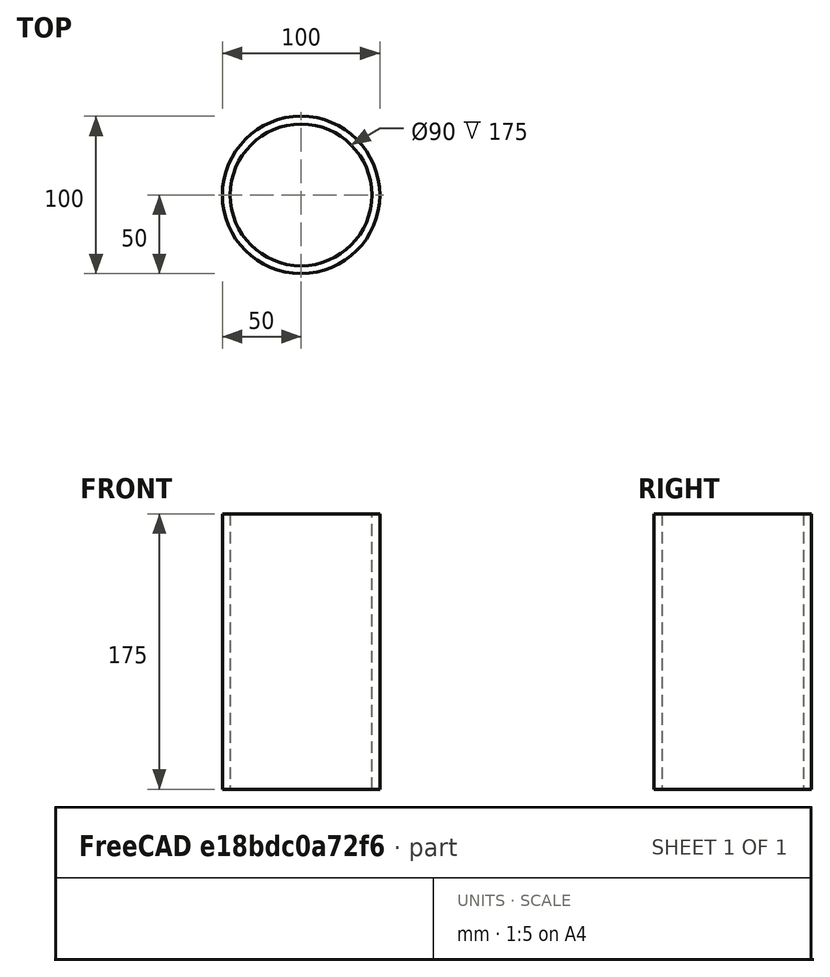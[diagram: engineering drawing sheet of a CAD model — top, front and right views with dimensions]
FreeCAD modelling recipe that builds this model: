
FCSTD DOCUMENT  (FreeCAD 0.18R16268 (Git))
Label: Cylindre
License: All rights reserved
LicenseURL: http://en.wikipedia.org/wiki/All_rights_reserved
objects: PartDesign::CoordinateSystem×2, App::DocumentObjectGroup×1, PartDesign::Plane×1, Sketcher::SketchObject×1, PartDesign::Pad×1, PartDesign::Body×1, App::Part×1
note: 7 computed .brp shape members not serialized (recipe doc carries the construction recipe); baked Part::Feature solids carry a one-line shape summary decoded from their .brp

FEATURE [App::DocumentObjectGroup] Constraints
FEATURE [PartDesign::CoordinateSystem] LCS
  AttacherType = Attacher::AttachEngine3D
  MapMode = 2
FEATURE [PartDesign::Plane] DatumPlane  label="Plan_XY"
  Length = 120
  MapMode = 2
  ResizeMode = 0
  Support = -> [LCS]
  Width = 120
FEATURE [Sketcher::SketchObject] Sketch
  MapMode = 5
  Support = -> [DatumPlane]
  sketch-geometry (4):
    g0: Circle CenterX=0 CenterY=-1e-16 CenterZ=0 NormalX=0 NormalY=0 NormalZ=1 AngleXU=0 Radius=45
    g1: Circle CenterX=0 CenterY=-1e-16 CenterZ=0 NormalX=0 NormalY=0 NormalZ=1 AngleXU=0 Radius=50
    g2: GeomPoint X=0 Y=45 Z=0
    g3: GeomPoint X=0 Y=50 Z=0
  constraints (8):
    c: Coincident(g0,g-1)
    c: Coincident(g1,g0)
    c: Diameter(g0) = 90
    c: PointOnObject(g2,g0)
    c: PointOnObject(g3,g1)
    c: PointOnObject(g3,g-2)
    c: PointOnObject(g2,g-2)
    c: DistanceY(g2,g3) = 5
FEATURE [PartDesign::Pad] Pad
  ClaimChildren = false
  Length = 175
  Length2 = 100
  Profile = -> Sketch
  Type = 0
FEATURE [PartDesign::Body] Body
  Group = -> [LCS,DatumPlane,Sketch,Pad]
  Origin = -> Origin001
  Tip = -> Pad
FEATURE [PartDesign::CoordinateSystem] LCS_0
  AttacherType = Attacher::AttachEngine3D
FEATURE [App::Part] Part
  Group = -> [Constraints,Body,LCS_0]
  Origin = -> Origin
